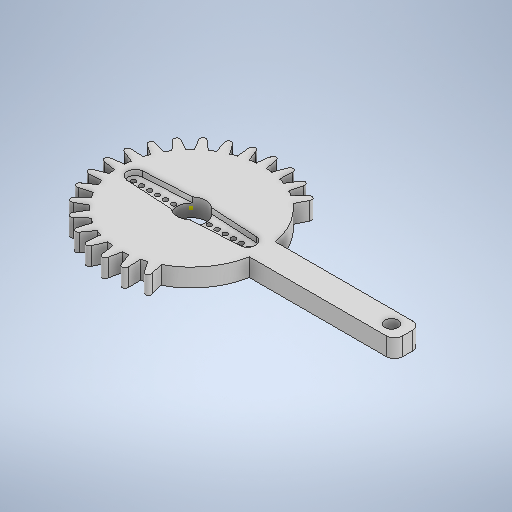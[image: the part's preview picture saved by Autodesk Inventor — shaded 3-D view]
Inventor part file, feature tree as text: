
AUTODESK INVENTOR PART (.ipt)
format: ipt  version: 2025.1 (Build 291241020, 241B)  size: 730,112 bytes
history: native  units: in
note: dims shown in document units (in); Inventor stores cm internally (conversion verified against a paired STEP export)
features: sketch x13, extrude x12, other x3, fillet x2, pattern_circular x1
ambient origin geometry x8: Origin, YZ Plane, XZ Plane, XY Plane, X Axis, Y Axis, Z Axis, Center Point
bodies: Solid1 (feature_tree)
feature tree (31):
  other  "servoMoldAssembly.iam"
  other  "block.ipt:1"
  other  "sg90horn.ipt:1"
  extrude  "Extrusion1"  Depth=0.3937in TaperAngle=0.0deg
  extrude  "Extrusion2"  Depth=0.3937in TaperAngle=0.0deg
  extrude  "Extrusion3"  Depth=0.0591in TaperAngle=0.0deg
  extrude  "Extrusion4"  Depth=0.0591in TaperAngle=0.0deg
  extrude  "Extrusion5"  Depth=1.9685in
  extrude  "Extrusion6"  Depth=0.3937in TaperAngle=0.0deg
  extrude  "Extrusion7"  Depth=0.3937in
  extrude  "Extrusion8"  Depth=0.0591in
  extrude  "Extrusion9"  Depth=0.3937in TaperAngle=240.0deg
  pattern_circular  "Circular Pattern1"  [2 undecoded]
  extrude  "Extrusion10"  Depth=0.0787in
  extrude  "Extrusion11"  Depth=0.0787in TaperAngle=0.0deg
  fillet  "Fillet1"  Radius=0.0787in
  extrude  "Extrusion12"  [1 undecoded]
  fillet  "Fillet2"  [1 undecoded]
  sketch  "Sketch15"  dims[d33=0.0787in d34=0.2362in d35=0.0in d36=0.0787in d37=0.2362in d38=0.0in d39=0.0787in]
  sketch  "Sketch3"  dims[d0=0.3937in d1=0.3937in d2=0.0in]
  sketch  "Sketch4"  dims[d3=0.2795in d4=0.3937in d5=0.0in]
  sketch  "Sketch5"  dims[d6=0.0591in d7=0.0in d8=0.0591in d9=0.0in]
  sketch  "Sketch6"  dims[d10=0.0591in d11=0.0in d12=0.0591in d13=0.0in]
  sketch  "Sketch7"  dims[d14=1.4173in d15=1.9685in]
  sketch  "Sketch8"  dims[d16=0.0in d17=0.3937in d18=0.0in]
  sketch  "Sketch9"  dims[d19=0.3937in d20=0.0in d21=0.0984in]
  sketch  "Sketch10"  dims[d22=0.1181in d23=0.0591in]
  sketch  "Sketch11"  dims[d24=0.3937in d25=0.0in d26=7.874in d27=240.0deg]
  sketch  "Sketch12"  dims[d29=0.2362in d30=0.0in]
  sketch  "Sketch13"  dims[d31=0.2362in]
  sketch  "Sketch14"  dims[d32=0.1299in]
note: 4 required parameter values undecoded (feature->parameter linkage not recoverable at this tier; creation-order binding heuristic only, values carry confidence <= 0.55)
